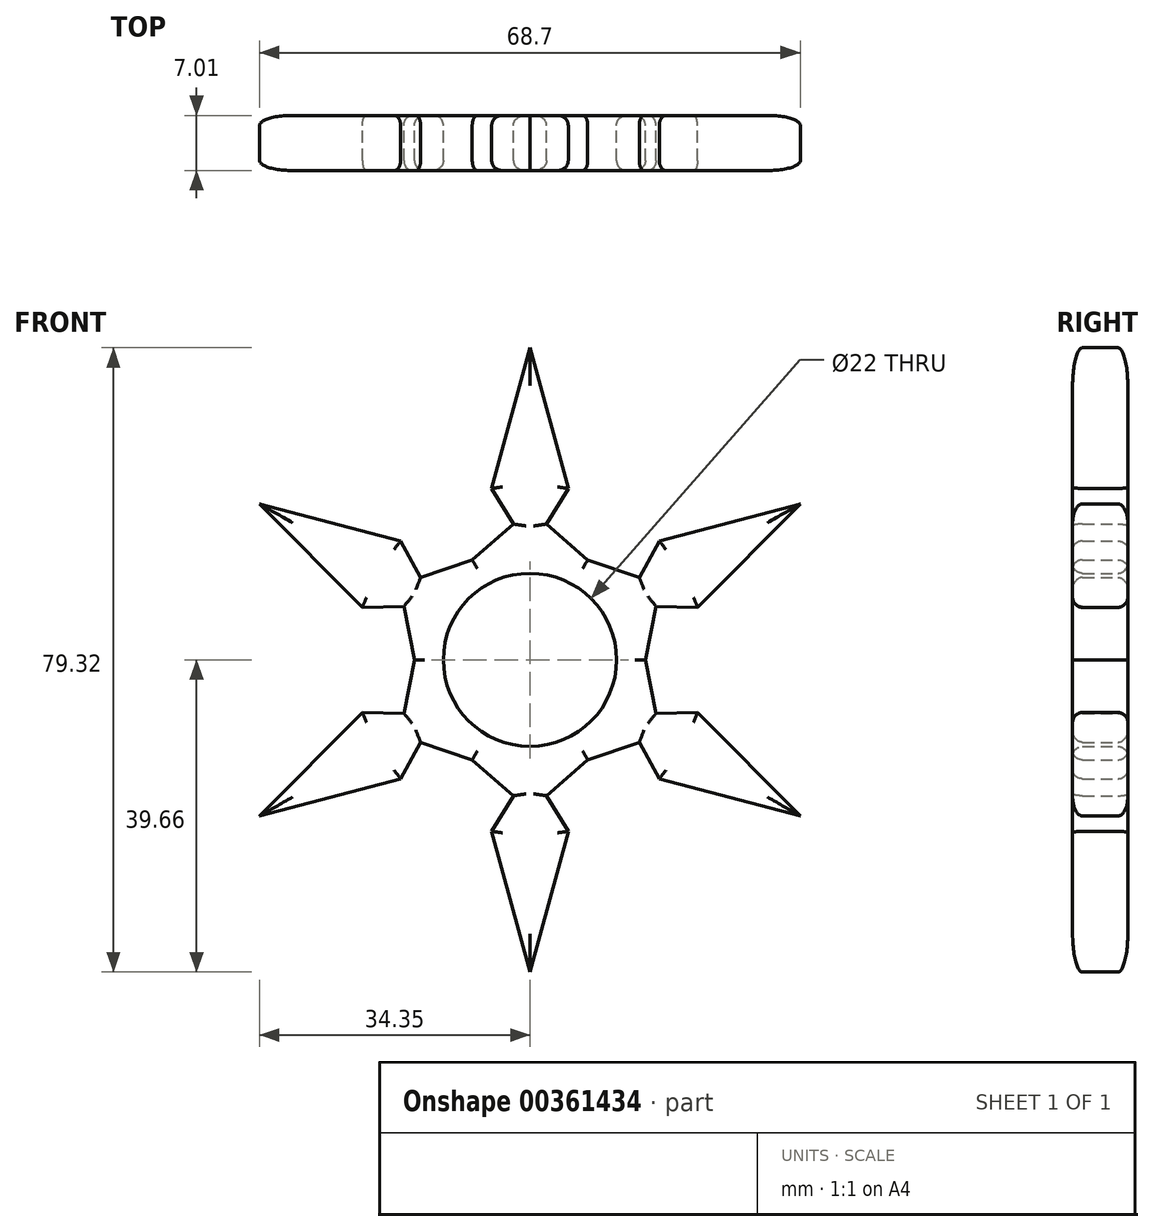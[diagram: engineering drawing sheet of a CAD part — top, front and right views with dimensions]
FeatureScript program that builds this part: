
annotation { "Feature Type Name" : "Feature", "Feature Type Description" : "" }
export const myFeature = defineFeature(function(context is Context, id is Id, definition is map)
    precondition{}
    {
        {
            var Q0;
            Q0=qCreatedBy(makeId("Front.planeOp"),FACE);
            var sketch = newSketch(context, id + "F0", { "sketchPlane" : qUnion([Q0])});
            skCircle(sketch, "E0.cCircle", {"center": v(0, 0) * mm, "radius": 12.7 * mm, "construction": true});
            skLineSegment(sketch, "E0.0", {"start": v(7.33, -12.7) * mm, "end": v(-7.33, -12.7) * mm});
            skLineSegment(sketch, "E0.1", {"start": v(-7.33, -12.7) * mm, "end": v(-14.66, 0) * mm});
            skLineSegment(sketch, "E0.2", {"start": v(-14.66, 0) * mm, "end": v(-7.33, 12.7) * mm});
            skLineSegment(sketch, "E0.3", {"start": v(-7.33, 12.7) * mm, "end": v(7.33, 12.7) * mm});
            skLineSegment(sketch, "E0.4", {"start": v(7.33, 12.7) * mm, "end": v(14.66, 0) * mm});
            skLineSegment(sketch, "E0.5", {"start": v(14.66, 0) * mm, "end": v(7.33, -12.7) * mm});
            skPoint(sketch, "E0.0.midPoint", {"position": v(0, -12.7) * mm});
            skLineSegment(sketch, "E1", {"start": v(-7.33, 12.7) * mm, "end": v(0, 39.66) * mm});
            skLineSegment(sketch, "E2", {"start": v(0, 39.66) * mm, "end": v(7.33, 12.7) * mm});
            skLineSegment(sketch, "E3", {"start": v(-7.33, 12.7) * mm, "end": v(-2.12, 17.26) * mm});
            skLineSegment(sketch, "E4", {"start": v(-2.12, 17.26) * mm, "end": v(-4.86, 21.77) * mm});
            skLineSegment(sketch, "E5", {"start": v(0, 0) * mm, "end": v(0, 7.4) * mm});
            skLineSegment(sketch, "E6.MirrorCS", {"start": v(2.12, 17.26) * mm, "end": v(4.86, 21.77) * mm});
            skLineSegment(sketch, "E7.MirrorCS", {"start": v(7.33, 12.7) * mm, "end": v(2.12, 17.26) * mm});
            skLineSegment(sketch, "E8.1.0", {"start": v(-14.66, 0) * mm, "end": v(-34.35, 19.83) * mm});
            skLineSegment(sketch, "E8.1.1", {"start": v(-34.35, 19.83) * mm, "end": v(-7.33, 12.7) * mm});
            skLineSegment(sketch, "E8.1.2", {"start": v(-13.9, 10.47) * mm, "end": v(-16.42, 15.1) * mm});
            skLineSegment(sketch, "E8.1.3", {"start": v(-16.01, 6.8) * mm, "end": v(-21.29, 6.67) * mm});
            skLineSegment(sketch, "E8.1.4", {"start": v(-14.66, 0) * mm, "end": v(-16.01, 6.8) * mm});
            skLineSegment(sketch, "E8.1.5", {"start": v(-7.33, 12.7) * mm, "end": v(-13.9, 10.47) * mm});
            skLineSegment(sketch, "E8.2.0", {"start": v(-7.33, -12.7) * mm, "end": v(-34.35, -19.83) * mm});
            skLineSegment(sketch, "E8.2.1", {"start": v(-34.35, -19.83) * mm, "end": v(-14.66, 0) * mm});
            skLineSegment(sketch, "E8.2.2", {"start": v(-16.01, -6.8) * mm, "end": v(-21.29, -6.67) * mm});
            skLineSegment(sketch, "E8.2.3", {"start": v(-13.9, -10.47) * mm, "end": v(-16.42, -15.1) * mm});
            skLineSegment(sketch, "E8.2.4", {"start": v(-7.33, -12.7) * mm, "end": v(-13.9, -10.47) * mm});
            skLineSegment(sketch, "E8.2.5", {"start": v(-14.66, 0) * mm, "end": v(-16.01, -6.8) * mm});
            skLineSegment(sketch, "E9.1.3.0", {"start": v(7.33, -12.7) * mm, "end": v(0, -39.66) * mm});
            skLineSegment(sketch, "E9.3.3.0", {"start": v(0, -39.66) * mm, "end": v(-7.33, -12.7) * mm});
            skLineSegment(sketch, "E9.6.3.0", {"start": v(-2.12, -17.26) * mm, "end": v(-4.86, -21.77) * mm});
            skLineSegment(sketch, "E9.9.3.0", {"start": v(2.12, -17.26) * mm, "end": v(4.86, -21.77) * mm});
            skLineSegment(sketch, "E9.12.3.0", {"start": v(7.33, -12.7) * mm, "end": v(2.12, -17.26) * mm});
            skLineSegment(sketch, "E9.15.3.0", {"start": v(-7.33, -12.7) * mm, "end": v(-2.12, -17.26) * mm});
            skLineSegment(sketch, "E9.1.4.0", {"start": v(14.66, 0) * mm, "end": v(34.35, -19.83) * mm});
            skLineSegment(sketch, "E9.3.4.0", {"start": v(34.35, -19.83) * mm, "end": v(7.33, -12.7) * mm});
            skLineSegment(sketch, "E9.6.4.0", {"start": v(13.9, -10.47) * mm, "end": v(16.42, -15.1) * mm});
            skLineSegment(sketch, "E9.9.4.0", {"start": v(16.01, -6.8) * mm, "end": v(21.29, -6.67) * mm});
            skLineSegment(sketch, "E9.12.4.0", {"start": v(14.66, 0) * mm, "end": v(16.01, -6.8) * mm});
            skLineSegment(sketch, "E9.15.4.0", {"start": v(7.33, -12.7) * mm, "end": v(13.9, -10.47) * mm});
            skLineSegment(sketch, "E9.1.5.0", {"start": v(7.33, 12.7) * mm, "end": v(34.35, 19.83) * mm});
            skLineSegment(sketch, "E9.3.5.0", {"start": v(34.35, 19.83) * mm, "end": v(14.66, 0) * mm});
            skLineSegment(sketch, "E9.6.5.0", {"start": v(16.01, 6.8) * mm, "end": v(21.29, 6.67) * mm});
            skLineSegment(sketch, "E9.9.5.0", {"start": v(13.9, 10.47) * mm, "end": v(16.42, 15.1) * mm});
            skLineSegment(sketch, "E9.12.5.0", {"start": v(7.33, 12.7) * mm, "end": v(13.9, 10.47) * mm});
            skLineSegment(sketch, "E9.15.5.0", {"start": v(14.66, 0) * mm, "end": v(16.01, 6.8) * mm});
            skCircle(sketch, "E10", {"center": v(0, 0) * mm, "radius": 11 * mm});
            skSolve(sketch);
        }
        {
            var Q0;
            Q0=makeQuery(id+"F0.imprint","IMPRINT",FACE,{"disambiguationData":[TD([[makeQuery(id+"F0.imprint","IMPRINT",EDGE,{"derivedFrom":sQuery(id+"F0.wireOp",EDGE,"E0.0")}),-1.0]])]});
            var Q1;
            Q1=makeQuery(id+"F0.imprint","IMPRINT",FACE,{"disambiguationData":[TD([[makeQuery(id+"F0.imprint","IMPRINT",EDGE,{"derivedFrom":sQuery(id+"F0.wireOp",EDGE,"E0.3")}),1.0]])]});
            var Q2;
            Q2=makeQuery(id+"F0.imprint","IMPRINT",FACE,{"disambiguationData":[TD([[makeQuery(id+"F0.imprint","IMPRINT",EDGE,{"derivedFrom":sQuery(id+"F0.wireOp",EDGE,"E0.2")}),1.0]])]});
            var Q3;
            Q3=makeQuery(id+"F0.imprint","IMPRINT",FACE,{"disambiguationData":[TD([[makeQuery(id+"F0.imprint","IMPRINT",EDGE,{"derivedFrom":sQuery(id+"F0.wireOp",EDGE,"E0.1")}),1.0]])]});
            var Q4;
            Q4=makeQuery(id+"F0.imprint","IMPRINT",FACE,{"disambiguationData":[TD([[makeQuery(id+"F0.imprint","IMPRINT",EDGE,{"derivedFrom":sQuery(id+"F0.wireOp",EDGE,"E0.0")}),1.0]])]});
            var Q5;
            Q5=makeQuery(id+"F0.imprint","IMPRINT",FACE,{"disambiguationData":[TD([[makeQuery(id+"F0.imprint","IMPRINT",EDGE,{"derivedFrom":sQuery(id+"F0.wireOp",EDGE,"E0.5")}),1.0]])]});
            var Q6;
            Q6=makeQuery(id+"F0.imprint","IMPRINT",FACE,{"disambiguationData":[TD([[makeQuery(id+"F0.imprint","IMPRINT",EDGE,{"derivedFrom":sQuery(id+"F0.wireOp",EDGE,"E0.4")}),1.0]])]});
            extrude(context, id + "F1", {"entities" : qUnion([Q0, Q1, Q2, Q3, Q4, Q5, Q6]), "depth" : 7 * mm, "offsetDistance" : 25.4 * mm});
        }
        {
            var Q0;
            Q0=makeQuery(id+"F1.opExtrude","CAP_FACE",FACE,{"disambiguationData":[OSD([sQuery(id+"F0.wireOp",EDGE,"E1"),sQuery(id+"F0.wireOp",EDGE,"E2"),sQuery(id+"F0.wireOp",EDGE,"E3"),sQuery(id+"F0.wireOp",EDGE,"E4"),sQuery(id+"F0.wireOp",EDGE,"E6.MirrorCS"),sQuery(id+"F0.wireOp",EDGE,"E7.MirrorCS"),sQuery(id+"F0.wireOp",EDGE,"E8.1.0"),sQuery(id+"F0.wireOp",EDGE,"E8.1.1"),sQuery(id+"F0.wireOp",EDGE,"E8.1.2"),sQuery(id+"F0.wireOp",EDGE,"E8.1.3"),sQuery(id+"F0.wireOp",EDGE,"E8.1.4"),sQuery(id+"F0.wireOp",EDGE,"E8.1.5"),sQuery(id+"F0.wireOp",EDGE,"E8.2.0"),sQuery(id+"F0.wireOp",EDGE,"E8.2.1"),sQuery(id+"F0.wireOp",EDGE,"E8.2.2"),sQuery(id+"F0.wireOp",EDGE,"E8.2.3"),sQuery(id+"F0.wireOp",EDGE,"E8.2.4"),sQuery(id+"F0.wireOp",EDGE,"E8.2.5"),sQuery(id+"F0.wireOp",EDGE,"E9.1.3.0"),sQuery(id+"F0.wireOp",EDGE,"E9.3.3.0"),sQuery(id+"F0.wireOp",EDGE,"E9.6.3.0"),sQuery(id+"F0.wireOp",EDGE,"E9.9.3.0"),sQuery(id+"F0.wireOp",EDGE,"E9.12.3.0"),sQuery(id+"F0.wireOp",EDGE,"E9.15.3.0"),sQuery(id+"F0.wireOp",EDGE,"E9.1.4.0"),sQuery(id+"F0.wireOp",EDGE,"E9.3.4.0"),sQuery(id+"F0.wireOp",EDGE,"E9.6.4.0"),sQuery(id+"F0.wireOp",EDGE,"E9.9.4.0"),sQuery(id+"F0.wireOp",EDGE,"E9.12.4.0"),sQuery(id+"F0.wireOp",EDGE,"E9.15.4.0"),sQuery(id+"F0.wireOp",EDGE,"E9.1.5.0"),sQuery(id+"F0.wireOp",EDGE,"E9.3.5.0"),sQuery(id+"F0.wireOp",EDGE,"E9.6.5.0"),sQuery(id+"F0.wireOp",EDGE,"E9.9.5.0"),sQuery(id+"F0.wireOp",EDGE,"E9.12.5.0"),sQuery(id+"F0.wireOp",EDGE,"E9.15.5.0"),sQuery(id+"F0.wireOp",EDGE,"E10")])],"isStart":false});
            var Q1;
            Q1=makeQuery(id+"F1.opExtrude","CAP_FACE",FACE,{"disambiguationData":[OSD([sQuery(id+"F0.wireOp",EDGE,"E1"),sQuery(id+"F0.wireOp",EDGE,"E2"),sQuery(id+"F0.wireOp",EDGE,"E3"),sQuery(id+"F0.wireOp",EDGE,"E4"),sQuery(id+"F0.wireOp",EDGE,"E6.MirrorCS"),sQuery(id+"F0.wireOp",EDGE,"E7.MirrorCS"),sQuery(id+"F0.wireOp",EDGE,"E8.1.0"),sQuery(id+"F0.wireOp",EDGE,"E8.1.1"),sQuery(id+"F0.wireOp",EDGE,"E8.1.2"),sQuery(id+"F0.wireOp",EDGE,"E8.1.3"),sQuery(id+"F0.wireOp",EDGE,"E8.1.4"),sQuery(id+"F0.wireOp",EDGE,"E8.1.5"),sQuery(id+"F0.wireOp",EDGE,"E8.2.0"),sQuery(id+"F0.wireOp",EDGE,"E8.2.1"),sQuery(id+"F0.wireOp",EDGE,"E8.2.2"),sQuery(id+"F0.wireOp",EDGE,"E8.2.3"),sQuery(id+"F0.wireOp",EDGE,"E8.2.4"),sQuery(id+"F0.wireOp",EDGE,"E8.2.5"),sQuery(id+"F0.wireOp",EDGE,"E9.1.3.0"),sQuery(id+"F0.wireOp",EDGE,"E9.3.3.0"),sQuery(id+"F0.wireOp",EDGE,"E9.6.3.0"),sQuery(id+"F0.wireOp",EDGE,"E9.9.3.0"),sQuery(id+"F0.wireOp",EDGE,"E9.12.3.0"),sQuery(id+"F0.wireOp",EDGE,"E9.15.3.0"),sQuery(id+"F0.wireOp",EDGE,"E9.1.4.0"),sQuery(id+"F0.wireOp",EDGE,"E9.3.4.0"),sQuery(id+"F0.wireOp",EDGE,"E9.6.4.0"),sQuery(id+"F0.wireOp",EDGE,"E9.9.4.0"),sQuery(id+"F0.wireOp",EDGE,"E9.12.4.0"),sQuery(id+"F0.wireOp",EDGE,"E9.15.4.0"),sQuery(id+"F0.wireOp",EDGE,"E9.1.5.0"),sQuery(id+"F0.wireOp",EDGE,"E9.3.5.0"),sQuery(id+"F0.wireOp",EDGE,"E9.6.5.0"),sQuery(id+"F0.wireOp",EDGE,"E9.9.5.0"),sQuery(id+"F0.wireOp",EDGE,"E9.12.5.0"),sQuery(id+"F0.wireOp",EDGE,"E9.15.5.0"),sQuery(id+"F0.wireOp",EDGE,"E10")])],"isStart":true});
            fillet(context, id + "F2", {"entities" : qUnion([Q0, Q1]), "radius" : 1.27 * mm, "tangentPropagation" : true, "allowEdgeOverflow" : false});
        }
    });
